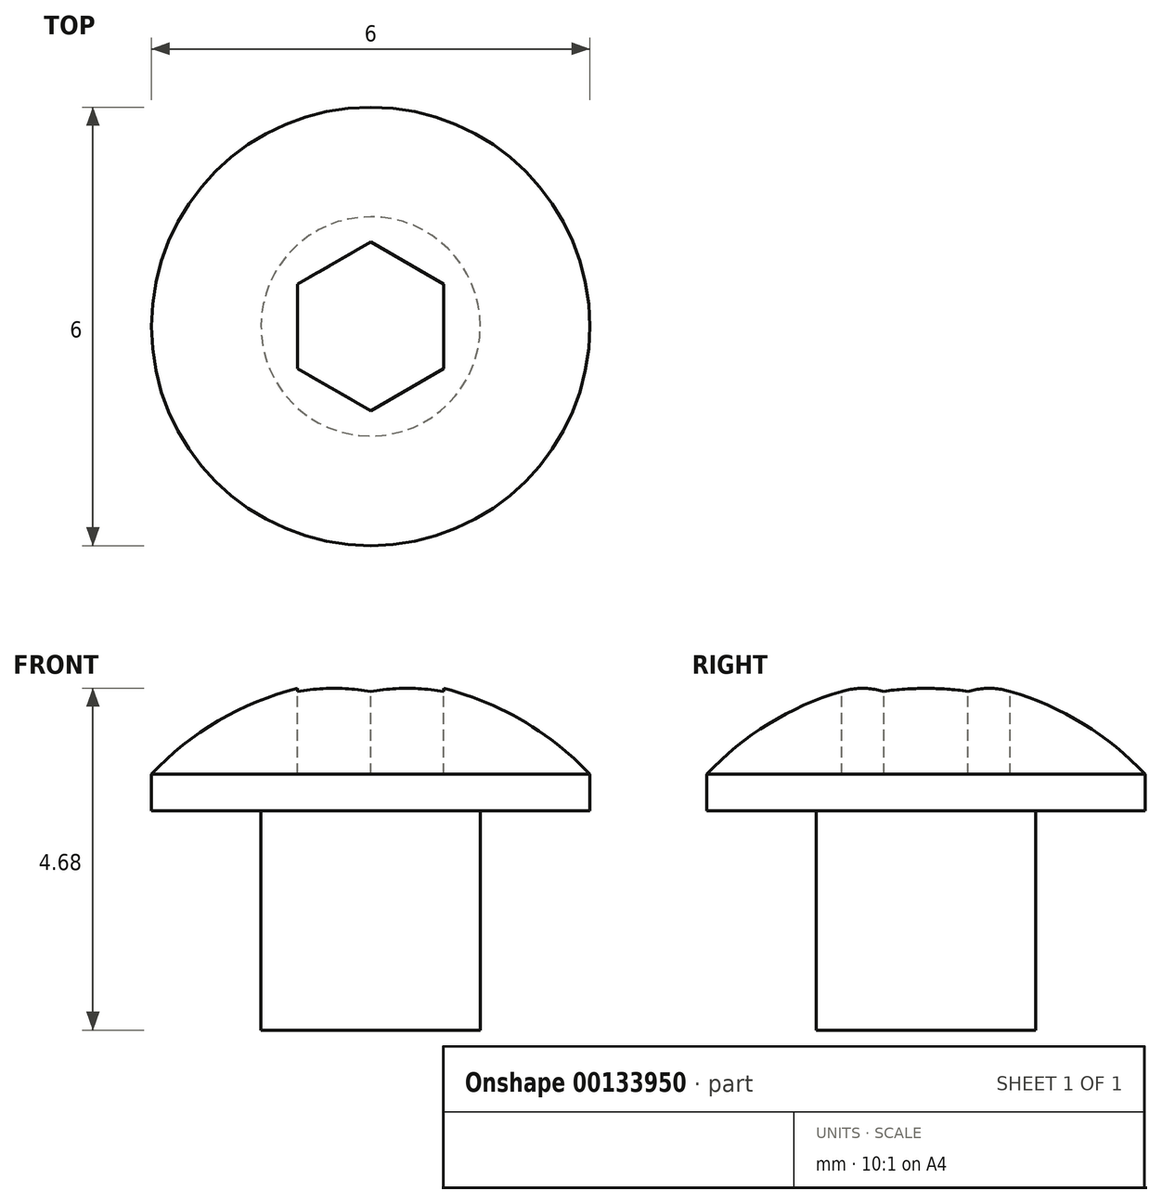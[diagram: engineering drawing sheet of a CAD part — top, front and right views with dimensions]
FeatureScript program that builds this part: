
annotation { "Feature Type Name" : "Feature", "Feature Type Description" : "" }
export const myFeature = defineFeature(function(context is Context, id is Id, definition is map)
    precondition{}
    {
        {
            var Q0;
            Q0=qCreatedBy(makeId("Front.planeOp"),FACE);
            var sketch = newSketch(context, id + "F0", { "sketchPlane" : qUnion([Q0])});
            skLineSegment(sketch, "E0", {"start": v(0, 11.74) * mm, "end": v(0, -9.83) * mm, "construction": true});
            skLineSegment(sketch, "E1", {"start": v(0, 0) * mm, "end": v(1.5, 0) * mm});
            skLineSegment(sketch, "E2", {"start": v(1.5, 0) * mm, "end": v(1.5, 3) * mm});
            skLineSegment(sketch, "E3", {"start": v(1.5, 3) * mm, "end": v(3, 3) * mm});
            skLineSegment(sketch, "E4", {"start": v(3, 3) * mm, "end": v(3, 3.5) * mm});
            skArc(sketch, "E5", {"start": v(3, 3.5) * mm, "mid": v(1.63, 4.46) * mm, "end": v(0, 4.8) * mm});
            skLineSegment(sketch, "E6", {"start": v(0, 4.8) * mm, "end": v(0, 0) * mm});
            skSolve(sketch);
        }
        {
            var Q0;
            Q0 = qSketchRegion(id + "F0", true);
            var Q1;
            Q1=sQuery(id+"F0.wireOp",EDGE,"E0");
            revolve(context, id + "F1", {"surfaceOperationType" : NewSurfaceOperationType.NEW, "entities" : qUnion([Q0]), "axis" : qUnion([Q1]), "revolveType" : RevolveType.FULL});
        }
        {
            var Q0;
            Q0=qCreatedBy(makeId("Top.planeOp"),FACE);
            cPlane(context, id + "F2", {"entities" : qUnion([Q0]), "cplaneType" : CPlaneType.OFFSET, "offset" : 6 * mm, "width" : 150 * mm, "height" : 150 * mm});
        }
        {
            var Q0;
            Q0=qCreatedBy(id+"F2.planeOp",FACE);
            var sketch = newSketch(context, id + "F3", { "sketchPlane" : qUnion([Q0])});
            skCircle(sketch, "E7.cCircle", {"center": v(0, 0) * mm, "radius": 1 * mm, "construction": true});
            skLineSegment(sketch, "E7.0", {"start": v(1, 0.58) * mm, "end": v(1, -0.58) * mm});
            skLineSegment(sketch, "E7.1", {"start": v(1, -0.58) * mm, "end": v(0, -1.15) * mm});
            skLineSegment(sketch, "E7.2", {"start": v(0, -1.15) * mm, "end": v(-1, -0.58) * mm});
            skLineSegment(sketch, "E7.3", {"start": v(-1, -0.58) * mm, "end": v(-1, 0.58) * mm});
            skLineSegment(sketch, "E7.4", {"start": v(-1, 0.58) * mm, "end": v(0, 1.15) * mm});
            skLineSegment(sketch, "E7.5", {"start": v(0, 1.15) * mm, "end": v(1, 0.58) * mm});
            skPoint(sketch, "E7.0.midPoint", {"position": v(1, 0) * mm});
            skSolve(sketch);
        }
        {
            var Q0;
            Q0 = qSketchRegion(id + "F3", true);
            extrude(context, id + "F4", {"entities" : qUnion([Q0]), "operationType" : NewBodyOperationType.REMOVE, "oppositeDirection" : true, "depth" : 2.5 * mm, "offsetDistance" : 25 * mm});
        }
    });
